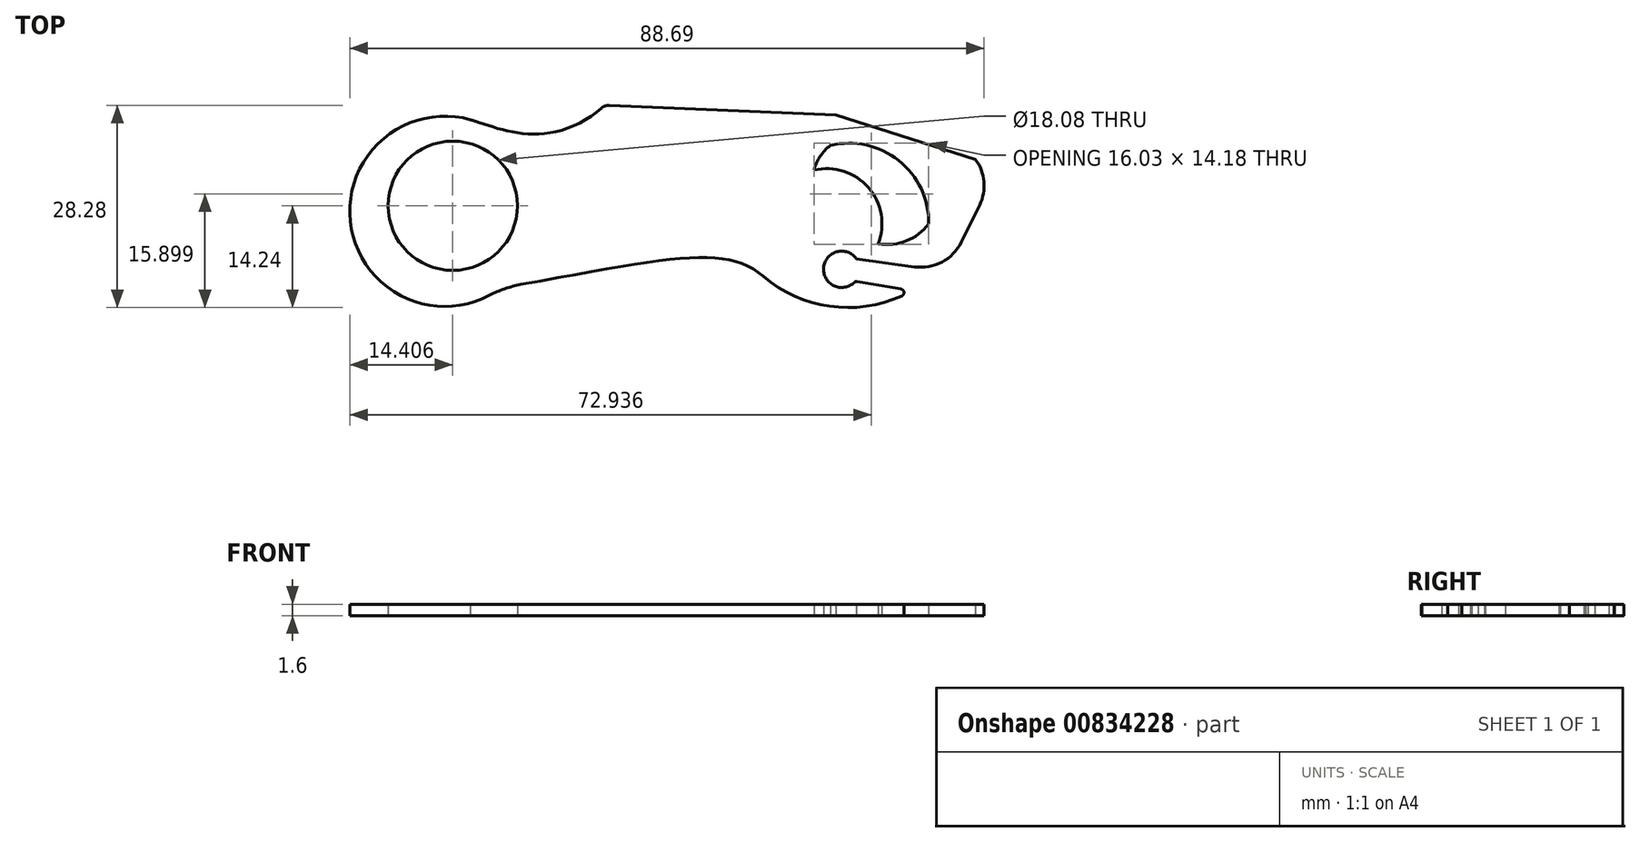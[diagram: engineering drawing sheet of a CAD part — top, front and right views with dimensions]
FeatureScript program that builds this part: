
annotation { "Feature Type Name" : "Feature", "Feature Type Description" : "" }
export const myFeature = defineFeature(function(context is Context, id is Id, definition is map)
    precondition{}
    {
        {
            var Q0;
            Q0=qCreatedBy(makeId("Top.planeOp"),FACE);
            var sketch = newSketch(context, id + "F0", { "sketchPlane" : qUnion([Q0]), "disableImprinting" : false});
            skCircle(sketch, "E0", {"center": v(-8.7, 0) * mm, "radius": 9.04 * mm});
            skPoint(sketch, "E1.1.internal.orphan", {"position": v(-15.09, -12.7) * mm});
            skPoint(sketch, "E1.2.internal.orphan", {"position": v(12.11, -12.7) * mm});
            skFitSpline(sketch, "E2", {"points": [v(-8.7, -12.7) * mm, v(38.9, -15.38) * mm, v(51.1, -59.61) * mm, v(41.65, -61.06) * mm], "startDerivative": vector(260.95, 45.13) * mm, "endDerivative": vector(-72.7, 2.9) * mm});
            skArc(sketch, "E3.filletArc", {"start": v(34.71, -9.86) * mm, "mid": v(44, -14.06) * mm, "end": v(54.08, -12.61) * mm});
            skArc(sketch, "E4", {"start": v(47.75, -7.42) * mm, "mid": v(43.15, -8.65) * mm, "end": v(47.44, -10.72) * mm});
            skLineSegment(sketch, "E5", {"start": v(64.97, 0.12) * mm, "end": v(62.42, -5.06) * mm});
            skPoint(sketch, "E6.visualSharp", {"position": v(67.84, 5.97) * mm});
            skArc(sketch, "E6.filletArc", {"start": v(64.97, 0.12) * mm, "mid": v(65.57, 3.37) * mm, "end": v(64.38, 6.46) * mm});
            skLineSegment(sketch, "E7", {"start": v(44.9, 12.7) * mm, "end": v(64.38, 6.46) * mm});
            skLineSegment(sketch, "E8", {"start": v(47.75, -7.42) * mm, "end": v(55.85, -8.54) * mm});
            skFitSpline(sketch, "E9", {"points": [v(-8.7, 12.7) * mm, v(8.32, 11.23) * mm, v(0, 17.15) * mm], "startDerivative": vector(21.26, -3.6) * mm, "endDerivative": vector(-135.52, -21.91) * mm});
            skLineSegment(sketch, "E10", {"start": v(13.16, 14.04) * mm, "end": v(44.9, 12.7) * mm});
            skPoint(sketch, "E11.visualSharp", {"position": v(12.51, 14.06) * mm});
            skArc(sketch, "E11.filletArc", {"start": v(13.16, 14.04) * mm, "mid": v(12.58, 13.95) * mm, "end": v(12.08, 13.64) * mm});
            skArc(sketch, "E12", {"start": v(-4.98, 11.62) * mm, "mid": v(-23.07, -1.55) * mm, "end": v(-3.57, -12.54) * mm});
            skPoint(sketch, "E13.visualSharp", {"position": v(-1.94, -11.51) * mm});
            skArc(sketch, "E13.filletArc", {"start": v(0.83, -11.01) * mm, "mid": v(-1.43, -11.6) * mm, "end": v(-3.57, -12.54) * mm});
            skPoint(sketch, "E14.0.visualSharp", {"position": v(60.4, -9.18) * mm});
            skArc(sketch, "E14.0.filletArc", {"start": v(55.85, -8.54) * mm, "mid": v(59.7, -7.86) * mm, "end": v(62.42, -5.06) * mm});
            skLineSegment(sketch, "E15", {"start": v(47.88, -10.59) * mm, "end": v(53.96, -11.65) * mm});
            skPoint(sketch, "E16.0.visualSharp", {"position": v(55.47, -11.91) * mm});
            skArc(sketch, "E16.0.filletArc", {"start": v(54.08, -12.61) * mm, "mid": v(54.38, -12.09) * mm, "end": v(53.96, -11.65) * mm});
            skPoint(sketch, "E17.0.visualSharp", {"position": v(47.61, -10.54) * mm});
            skArc(sketch, "E17.0.filletArc", {"start": v(47.88, -10.59) * mm, "mid": v(47.65, -10.6) * mm, "end": v(47.44, -10.72) * mm});
            skSolve(sketch);
        }
        {
            var Q0;
            Q0=makeQuery(id+"F0.imprint","IMPRINT",FACE,{"disambiguationData":[TD([[makeQuery(id+"F0.imprint","IMPRINT",EDGE,{"derivedFrom":sQuery(id+"F0.wireOp",EDGE,"E0")}),-1.0]])]});
            extrude(context, id + "F1", {"entities" : qUnion([Q0]), "depth" : 1.6 * mm, "offsetDistance" : 25.4 * mm});
        }
        {
            var Q0;
            Q0=qCreatedBy(makeId("Top.planeOp"),FACE);
            var sketch = newSketch(context, id + "F2", { "sketchPlane" : qUnion([Q0])});
            skArc(sketch, "E18", {"start": v(50.79, -5.33) * mm, "mid": v(49.42, 2.54) * mm, "end": v(41.82, 4.98) * mm});
            skArc(sketch, "E19", {"start": v(57.85, -2.53) * mm, "mid": v(53.65, 6.32) * mm, "end": v(44.1, 8.44) * mm});
            skArc(sketch, "E20", {"start": v(44.1, 8.44) * mm, "mid": v(42.67, 6.9) * mm, "end": v(41.82, 4.98) * mm});
            skArc(sketch, "E21", {"start": v(50.79, -5.33) * mm, "mid": v(54.71, -4.92) * mm, "end": v(57.85, -2.53) * mm});
            skSolve(sketch);
        }
        {
            var Q0;
            Q0 = qSketchRegion(id + "F2", true);
            extrude(context, id + "F3", {"entities" : qUnion([Q0]), "operationType" : NewBodyOperationType.REMOVE, "endBound" : BoundingType.UP_TO_NEXT, "depth" : 26.16 * mm, "offsetDistance" : 25.4 * mm});
        }
    });
